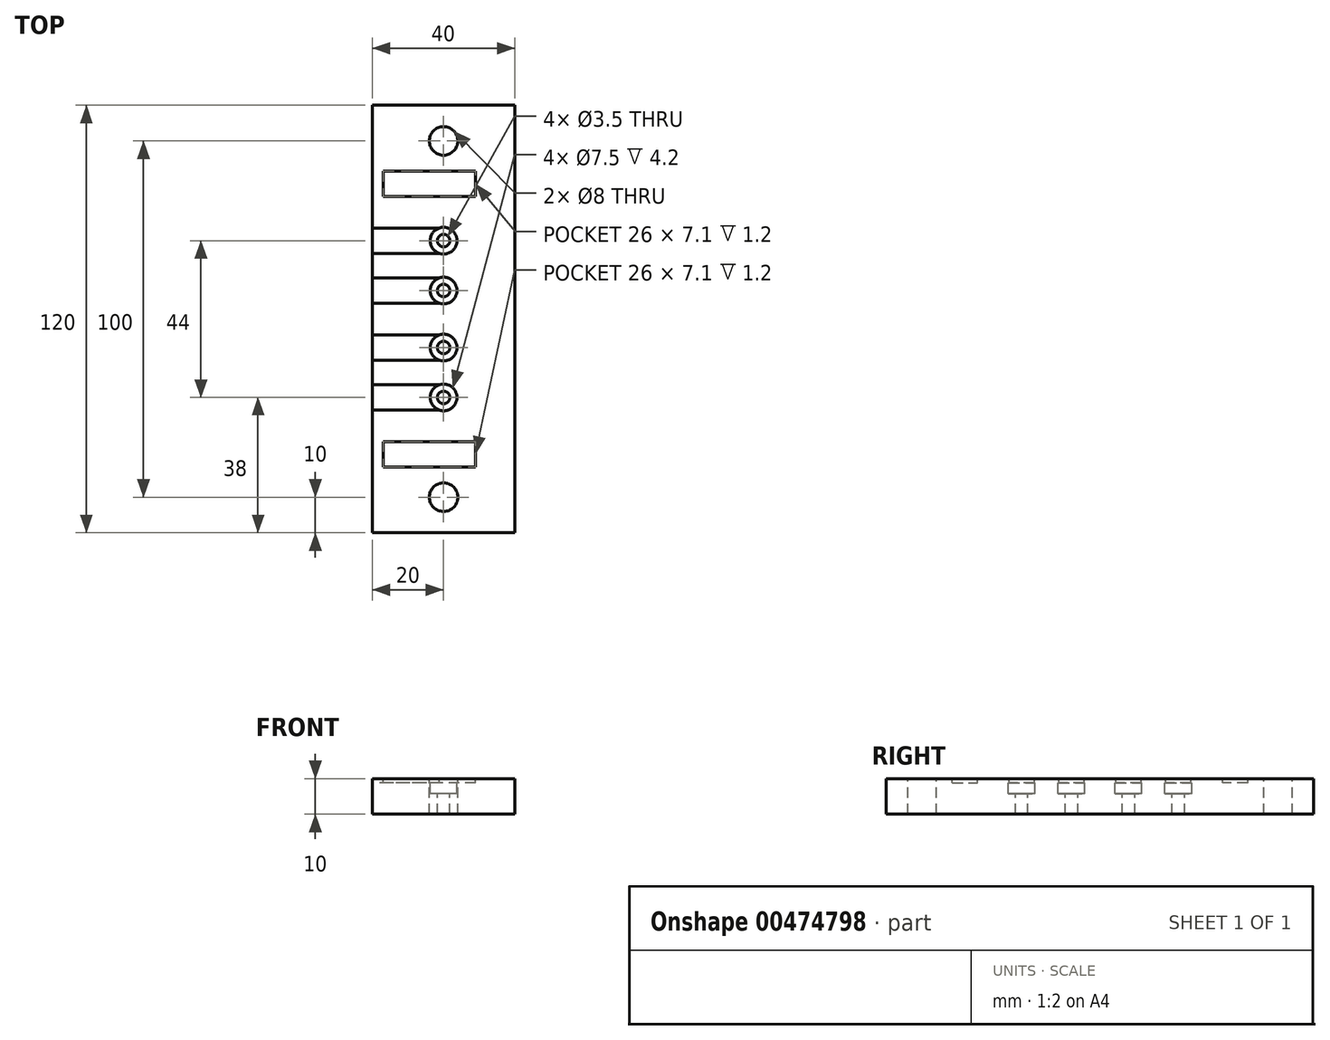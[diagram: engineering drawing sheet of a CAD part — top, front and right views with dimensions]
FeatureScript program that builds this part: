
annotation { "Feature Type Name" : "Feature", "Feature Type Description" : "" }
export const myFeature = defineFeature(function(context is Context, id is Id, definition is map)
    precondition{}
    {
        {
            var Q0;
            Q0=qCreatedBy(makeId("Top.planeOp"),FACE);
            var sketch = newSketch(context, id + "F0", { "sketchPlane" : qUnion([Q0])});
            skLineSegment(sketch, "E0.bottom", {"start": v(20, -60) * mm, "end": v(-20, -60) * mm});
            skLineSegment(sketch, "E0.top", {"start": v(20, 60) * mm, "end": v(-20, 60) * mm});
            skLineSegment(sketch, "E0.left", {"start": v(20, -60) * mm, "end": v(20, 60) * mm});
            skLineSegment(sketch, "E0.right", {"start": v(-20, -60) * mm, "end": v(-20, 60) * mm});
            skPoint(sketch, "E0.middle", {"position": v(0, 0) * mm});
            skCircle(sketch, "E1", {"center": v(0, 50) * mm, "radius": 4 * mm});
            skCircle(sketch, "E2.MirrorC", {"center": v(0, -50) * mm, "radius": 4 * mm});
            skLineSegment(sketch, "E3", {"start": v(0, 4.45) * mm, "end": v(-20, 4.45) * mm});
            skLineSegment(sketch, "E4", {"start": v(0, 11.55) * mm, "end": v(-20, 11.55) * mm});
            skLineSegment(sketch, "E5", {"start": v(0, 18.45) * mm, "end": v(-20, 18.45) * mm});
            skLineSegment(sketch, "E6", {"start": v(0, 25.55) * mm, "end": v(-20, 25.55) * mm});
            skLineSegment(sketch, "E7.MirrorCS", {"start": v(0, -4.45) * mm, "end": v(-20, -4.45) * mm});
            skLineSegment(sketch, "E8.MirrorCS", {"start": v(0, -11.55) * mm, "end": v(-20, -11.55) * mm});
            skLineSegment(sketch, "E9.MirrorCS", {"start": v(0, -18.45) * mm, "end": v(-20, -18.45) * mm});
            skLineSegment(sketch, "E10.MirrorCS", {"start": v(0, -25.55) * mm, "end": v(-20, -25.55) * mm});
            skLineSegment(sketch, "E11", {"start": v(0, 25.55) * mm, "end": v(0, 18.45) * mm});
            skLineSegment(sketch, "E12", {"start": v(0, 11.55) * mm, "end": v(0, 4.45) * mm});
            skLineSegment(sketch, "E13", {"start": v(0, -4.45) * mm, "end": v(0, -11.55) * mm});
            skLineSegment(sketch, "E14", {"start": v(0, -18.45) * mm, "end": v(0, -25.55) * mm});
            skCircle(sketch, "E15", {"center": v(0, 22) * mm, "radius": 3.75 * mm});
            skCircle(sketch, "E16", {"center": v(0, 8) * mm, "radius": 3.75 * mm});
            skCircle(sketch, "E17", {"center": v(0, 22) * mm, "radius": 1.75 * mm});
            skCircle(sketch, "E18", {"center": v(0, 8) * mm, "radius": 1.75 * mm});
            skCircle(sketch, "E19.MirrorC", {"center": v(0, -8) * mm, "radius": 3.75 * mm});
            skCircle(sketch, "E20.MirrorC", {"center": v(0, -8) * mm, "radius": 1.75 * mm});
            skCircle(sketch, "E21.MirrorC", {"center": v(0, -22) * mm, "radius": 3.75 * mm});
            skCircle(sketch, "E22.MirrorC", {"center": v(0, -22) * mm, "radius": 1.75 * mm});
            skLineSegment(sketch, "E23", {"start": v(9, 41.5) * mm, "end": v(9, 34.4) * mm});
            skLineSegment(sketch, "E24", {"start": v(9, 41.5) * mm, "end": v(-17, 41.5) * mm});
            skLineSegment(sketch, "E25", {"start": v(9, 34.4) * mm, "end": v(-17, 34.4) * mm});
            skLineSegment(sketch, "E26", {"start": v(-17, 41.5) * mm, "end": v(-17, 34.4) * mm});
            skLineSegment(sketch, "E27.MirrorCS", {"start": v(9, -34.4) * mm, "end": v(-17, -34.4) * mm});
            skLineSegment(sketch, "E28.MirrorCS", {"start": v(9, -41.5) * mm, "end": v(9, -34.4) * mm});
            skLineSegment(sketch, "E29.MirrorCS", {"start": v(9, -41.5) * mm, "end": v(-17, -41.5) * mm});
            skLineSegment(sketch, "E30.MirrorCS", {"start": v(-17, -41.5) * mm, "end": v(-17, -34.4) * mm});
            skSolve(sketch);
        }
        {
            var Q0;
            Q0 = qSketchRegion(id + "F0", true);
            var Q1;
            {var subQ0=sQuery(id+"F0.wireOp",EDGE,"E11");var subQ1=sQuery(id+"F0.wireOp",EDGE,"E5");var subQ2=makeQuery(id+"F0.imprint","INTERSECT",VERTEX,{"derivedFrom":[subQ1,subQ0]});Q1=makeQuery(id+"F0.imprint","IMPRINT",FACE,{"disambiguationData":[TD([[makeQuery(id+"F0.imprint","IMPRINT",EDGE,{"disambiguationData":[TD([[subQ2,-1.0]])],"derivedFrom":subQ1}),-1.0]])]});}
            var Q2;
            {var subQ0=sQuery(id+"F0.wireOp",EDGE,"E11");var subQ1=sQuery(id+"F0.wireOp",EDGE,"E5");var subQ2=makeQuery(id+"F0.imprint","INTERSECT",VERTEX,{"derivedFrom":[subQ1,subQ0]});Q2=makeQuery(id+"F0.imprint","IMPRINT",FACE,{"disambiguationData":[TD([[makeQuery(id+"F0.imprint","IMPRINT",EDGE,{"disambiguationData":[TD([[subQ2,-1.0]])],"derivedFrom":subQ1}),1.0]])]});}
            var Q3;
            {var subQ0=sQuery(id+"F0.wireOp",EDGE,"E12");var subQ1=sQuery(id+"F0.wireOp",EDGE,"E3");var subQ2=makeQuery(id+"F0.imprint","INTERSECT",VERTEX,{"derivedFrom":[subQ1,subQ0]});Q3=makeQuery(id+"F0.imprint","IMPRINT",FACE,{"disambiguationData":[TD([[makeQuery(id+"F0.imprint","IMPRINT",EDGE,{"disambiguationData":[TD([[subQ2,-1.0]])],"derivedFrom":subQ1}),1.0]])]});}
            var Q4;
            {var subQ0=sQuery(id+"F0.wireOp",EDGE,"E12");var subQ1=sQuery(id+"F0.wireOp",EDGE,"E3");var subQ2=makeQuery(id+"F0.imprint","INTERSECT",VERTEX,{"derivedFrom":[subQ1,subQ0]});Q4=makeQuery(id+"F0.imprint","IMPRINT",FACE,{"disambiguationData":[TD([[makeQuery(id+"F0.imprint","IMPRINT",EDGE,{"disambiguationData":[TD([[subQ2,-1.0]])],"derivedFrom":subQ1}),-1.0]])]});}
            var Q5;
            {var subQ0=sQuery(id+"F0.wireOp",EDGE,"E13");var subQ5=sQuery(id+"F0.wireOp",EDGE,"E7.MirrorCS");var subQ6=makeQuery(id+"F0.imprint","INTERSECT",VERTEX,{"derivedFrom":[subQ5,subQ0]});Q5=makeQuery(id+"F0.imprint","IMPRINT",FACE,{"disambiguationData":[TD([[makeQuery(id+"F0.imprint","IMPRINT",EDGE,{"disambiguationData":[TD([[subQ6,-1.0]])],"derivedFrom":subQ5}),1.0]])]});}
            var Q6;
            {var subQ0=sQuery(id+"F0.wireOp",EDGE,"E13");var subQ5=sQuery(id+"F0.wireOp",EDGE,"E7.MirrorCS");var subQ6=makeQuery(id+"F0.imprint","INTERSECT",VERTEX,{"derivedFrom":[subQ5,subQ0]});Q6=makeQuery(id+"F0.imprint","IMPRINT",FACE,{"disambiguationData":[TD([[makeQuery(id+"F0.imprint","IMPRINT",EDGE,{"disambiguationData":[TD([[subQ6,-1.0]])],"derivedFrom":subQ5}),-1.0]])]});}
            var Q7;
            {var subQ0=sQuery(id+"F0.wireOp",EDGE,"E14");var subQ1=sQuery(id+"F0.wireOp",EDGE,"E9.MirrorCS");var subQ2=makeQuery(id+"F0.imprint","INTERSECT",VERTEX,{"derivedFrom":[subQ1,subQ0]});Q7=makeQuery(id+"F0.imprint","IMPRINT",FACE,{"disambiguationData":[TD([[makeQuery(id+"F0.imprint","IMPRINT",EDGE,{"disambiguationData":[TD([[subQ2,-1.0]])],"derivedFrom":subQ1}),-1.0]])]});}
            var Q8;
            {var subQ0=sQuery(id+"F0.wireOp",EDGE,"E14");var subQ1=sQuery(id+"F0.wireOp",EDGE,"E9.MirrorCS");var subQ2=makeQuery(id+"F0.imprint","INTERSECT",VERTEX,{"derivedFrom":[subQ1,subQ0]});Q8=makeQuery(id+"F0.imprint","IMPRINT",FACE,{"disambiguationData":[TD([[makeQuery(id+"F0.imprint","IMPRINT",EDGE,{"disambiguationData":[TD([[subQ2,-1.0]])],"derivedFrom":subQ1}),1.0]])]});}
            var Q9;
            Q9=makeQuery(id+"F0.imprint","IMPRINT",FACE,{"disambiguationData":[TD([[makeQuery(id+"F0.imprint","IMPRINT",EDGE,{"derivedFrom":sQuery(id+"F0.wireOp",EDGE,"E23")}),-1.0]])]});
            var Q10;
            Q10=makeQuery(id+"F0.imprint","IMPRINT",FACE,{"disambiguationData":[TD([[makeQuery(id+"F0.imprint","IMPRINT",EDGE,{"derivedFrom":sQuery(id+"F0.wireOp",EDGE,"E27.MirrorCS")}),1.0]])]});
            extrude(context, id + "F1", {"entities" : qUnion([Q0, Q1, Q2, Q3, Q4, Q5, Q6, Q7, Q8, Q9, Q10]), "oppositeDirection" : true, "depth" : 10 * mm});
        }
        {
            var Q0;
            {var subQ0=sQuery(id+"F0.wireOp",EDGE,"E5");var subQ1=sQuery(id+"F0.wireOp",EDGE,"E0.right");var subQ2=makeQuery(id+"F0.imprint","INTERSECT",VERTEX,{"derivedFrom":[subQ1,subQ0]});Q0=makeQuery(id+"F0.imprint","IMPRINT",FACE,{"disambiguationData":[TD([[makeQuery(id+"F0.imprint","IMPRINT",EDGE,{"disambiguationData":[TD([[subQ2,-1.0]])],"derivedFrom":subQ1}),-1.0]])]});}
            var Q1;
            {var subQ0=sQuery(id+"F0.wireOp",EDGE,"E3");var subQ1=sQuery(id+"F0.wireOp",EDGE,"E0.right");var subQ2=makeQuery(id+"F0.imprint","INTERSECT",VERTEX,{"derivedFrom":[subQ1,subQ0]});Q1=makeQuery(id+"F0.imprint","IMPRINT",FACE,{"disambiguationData":[TD([[makeQuery(id+"F0.imprint","IMPRINT",EDGE,{"disambiguationData":[TD([[subQ2,-1.0]])],"derivedFrom":subQ1}),-1.0]])]});}
            var Q2;
            {var subQ0=sQuery(id+"F0.wireOp",EDGE,"E7.MirrorCS");var subQ1=sQuery(id+"F0.wireOp",EDGE,"E0.right");var subQ2=makeQuery(id+"F0.imprint","INTERSECT",VERTEX,{"derivedFrom":[subQ1,subQ0]});Q2=makeQuery(id+"F0.imprint","IMPRINT",FACE,{"disambiguationData":[TD([[makeQuery(id+"F0.imprint","IMPRINT",EDGE,{"disambiguationData":[TD([[subQ2,1.0]])],"derivedFrom":subQ1}),-1.0]])]});}
            var Q3;
            {var subQ0=sQuery(id+"F0.wireOp",EDGE,"E9.MirrorCS");var subQ1=sQuery(id+"F0.wireOp",EDGE,"E0.right");var subQ2=makeQuery(id+"F0.imprint","INTERSECT",VERTEX,{"derivedFrom":[subQ1,subQ0]});Q3=makeQuery(id+"F0.imprint","IMPRINT",FACE,{"disambiguationData":[TD([[makeQuery(id+"F0.imprint","IMPRINT",EDGE,{"disambiguationData":[TD([[subQ2,1.0]])],"derivedFrom":subQ1}),-1.0]])]});}
            var Q4;
            {var subQ0=sQuery(id+"F0.wireOp",EDGE,"Xl93sdzD-eEae-eb8l-Ilgp-bASjA5XagbHD");Q4=makeQuery(id+"F0.imprint","IMPRINT",FACE,{"disambiguationData":[TD([[makeQuery(id+"F0.imprint","IMPRINT",EDGE,{"derivedFrom":subQ0}),1.0]])]});}
            var Q5;
            Q5=makeQuery(id+"F0.imprint","IMPRINT",FACE,{"disambiguationData":[TD([[makeQuery(id+"F0.imprint","IMPRINT",EDGE,{"derivedFrom":sQuery(id+"F0.wireOp",EDGE,"e3db9e65-02f9-480d-be1d-b48fd13390820.MirrorCS")}),1.0]])]});
            var Q6;
            Q6=makeQuery(id+"F0.imprint","IMPRINT",FACE,{"disambiguationData":[TD([[makeQuery(id+"F0.imprint","IMPRINT",EDGE,{"derivedFrom":sQuery(id+"F0.wireOp",EDGE,"E23")}),-1.0]])]});
            var Q7;
            Q7=makeQuery(id+"F0.imprint","IMPRINT",FACE,{"disambiguationData":[TD([[makeQuery(id+"F0.imprint","IMPRINT",EDGE,{"derivedFrom":sQuery(id+"F0.wireOp",EDGE,"E27.MirrorCS")}),1.0]])]});
            extrude(context, id + "F2", {"entities" : qUnion([Q0, Q1, Q2, Q3, Q4, Q5, Q6, Q7]), "operationType" : NewBodyOperationType.REMOVE, "oppositeDirection" : true, "depth" : 1.2 * mm});
        }
        {
            var Q0;
            {var subQ0=sQuery(id+"F0.wireOp",EDGE,"E11");var subQ1=sQuery(id+"F0.wireOp",EDGE,"E5");var subQ2=makeQuery(id+"F0.imprint","INTERSECT",VERTEX,{"derivedFrom":[subQ1,subQ0]});Q0=makeQuery(id+"F0.imprint","IMPRINT",FACE,{"disambiguationData":[TD([[makeQuery(id+"F0.imprint","IMPRINT",EDGE,{"disambiguationData":[TD([[subQ2,-1.0]])],"derivedFrom":subQ1}),-1.0]])]});}
            var Q1;
            {var subQ0=sQuery(id+"F0.wireOp",EDGE,"E11");var subQ1=sQuery(id+"F0.wireOp",EDGE,"E5");var subQ2=makeQuery(id+"F0.imprint","INTERSECT",VERTEX,{"derivedFrom":[subQ1,subQ0]});Q1=makeQuery(id+"F0.imprint","IMPRINT",FACE,{"disambiguationData":[TD([[makeQuery(id+"F0.imprint","IMPRINT",EDGE,{"disambiguationData":[TD([[subQ2,-1.0]])],"derivedFrom":subQ1}),1.0]])]});}
            var Q2;
            {var subQ0=sQuery(id+"F0.wireOp",EDGE,"E12");var subQ1=sQuery(id+"F0.wireOp",EDGE,"E3");var subQ2=makeQuery(id+"F0.imprint","INTERSECT",VERTEX,{"derivedFrom":[subQ1,subQ0]});Q2=makeQuery(id+"F0.imprint","IMPRINT",FACE,{"disambiguationData":[TD([[makeQuery(id+"F0.imprint","IMPRINT",EDGE,{"disambiguationData":[TD([[subQ2,-1.0]])],"derivedFrom":subQ1}),-1.0]])]});}
            var Q3;
            {var subQ0=sQuery(id+"F0.wireOp",EDGE,"E12");var subQ1=sQuery(id+"F0.wireOp",EDGE,"E3");var subQ2=makeQuery(id+"F0.imprint","INTERSECT",VERTEX,{"derivedFrom":[subQ1,subQ0]});Q3=makeQuery(id+"F0.imprint","IMPRINT",FACE,{"disambiguationData":[TD([[makeQuery(id+"F0.imprint","IMPRINT",EDGE,{"disambiguationData":[TD([[subQ2,-1.0]])],"derivedFrom":subQ1}),1.0]])]});}
            var Q4;
            {var subQ0=sQuery(id+"F0.wireOp",EDGE,"E13");var subQ5=sQuery(id+"F0.wireOp",EDGE,"E7.MirrorCS");var subQ6=makeQuery(id+"F0.imprint","INTERSECT",VERTEX,{"derivedFrom":[subQ5,subQ0]});Q4=makeQuery(id+"F0.imprint","IMPRINT",FACE,{"disambiguationData":[TD([[makeQuery(id+"F0.imprint","IMPRINT",EDGE,{"disambiguationData":[TD([[subQ6,-1.0]])],"derivedFrom":subQ5}),1.0]])]});}
            var Q5;
            {var subQ0=sQuery(id+"F0.wireOp",EDGE,"E13");var subQ5=sQuery(id+"F0.wireOp",EDGE,"E7.MirrorCS");var subQ6=makeQuery(id+"F0.imprint","INTERSECT",VERTEX,{"derivedFrom":[subQ5,subQ0]});Q5=makeQuery(id+"F0.imprint","IMPRINT",FACE,{"disambiguationData":[TD([[makeQuery(id+"F0.imprint","IMPRINT",EDGE,{"disambiguationData":[TD([[subQ6,-1.0]])],"derivedFrom":subQ5}),-1.0]])]});}
            var Q6;
            {var subQ0=sQuery(id+"F0.wireOp",EDGE,"E14");var subQ1=sQuery(id+"F0.wireOp",EDGE,"E9.MirrorCS");var subQ2=makeQuery(id+"F0.imprint","INTERSECT",VERTEX,{"derivedFrom":[subQ1,subQ0]});Q6=makeQuery(id+"F0.imprint","IMPRINT",FACE,{"disambiguationData":[TD([[makeQuery(id+"F0.imprint","IMPRINT",EDGE,{"disambiguationData":[TD([[subQ2,-1.0]])],"derivedFrom":subQ1}),-1.0]])]});}
            var Q7;
            {var subQ0=sQuery(id+"F0.wireOp",EDGE,"E14");var subQ1=sQuery(id+"F0.wireOp",EDGE,"E9.MirrorCS");var subQ2=makeQuery(id+"F0.imprint","INTERSECT",VERTEX,{"derivedFrom":[subQ1,subQ0]});Q7=makeQuery(id+"F0.imprint","IMPRINT",FACE,{"disambiguationData":[TD([[makeQuery(id+"F0.imprint","IMPRINT",EDGE,{"disambiguationData":[TD([[subQ2,-1.0]])],"derivedFrom":subQ1}),1.0]])]});}
            extrude(context, id + "F3", {"entities" : qUnion([Q0, Q1, Q2, Q3, Q4, Q5, Q6, Q7]), "operationType" : NewBodyOperationType.REMOVE, "oppositeDirection" : true, "depth" : 4.2 * mm});
        }
    });
